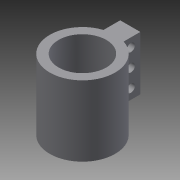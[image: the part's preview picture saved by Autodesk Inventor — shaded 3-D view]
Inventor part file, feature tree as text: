
AUTODESK INVENTOR PART (.ipt)
format: ipt  version: 2013 SP2 (Build 170200200, 200)  size: 125,952 bytes
history: native  units: mm
features: extrude x3, sketch x2, revolve x1
ambient origin geometry x8: Origin, YZ Plane, XZ Plane, XY Plane, X Axis, Y Axis, Z Axis, Center Point
bodies: Solid1 (feature_tree)
feature tree (6):
  revolve  "Revolution1"  [1 undecoded]
  extrude  "Extrusion1"  Depth=3.2mm
  extrude  "Extrusion2"  Depth=3.2mm
  extrude  "Extrusion3"  Depth=7.0mm
  sketch  "Sketch3"  dims[d7=90.0deg d20=8.0mm d21=0.0mm]
  sketch  "Sketch4"  dims[d28=19.0mm d29=3.2mm d30=3.2mm d31=7.0mm d32=10.0mm d33=0.0mm d34=3.75mm d36=13.0mm d47=15.0mm d49=4.0mm d50=4.0mm d51=10.0mm d52=0.0mm d63=28.0mm d65=9.5mm d66=16.057029mm d67=3.2mm d68=7.0mm]
note: 1 required parameter value undecoded (feature->parameter linkage not recoverable at this tier; creation-order binding heuristic only, values carry confidence <= 0.55)
